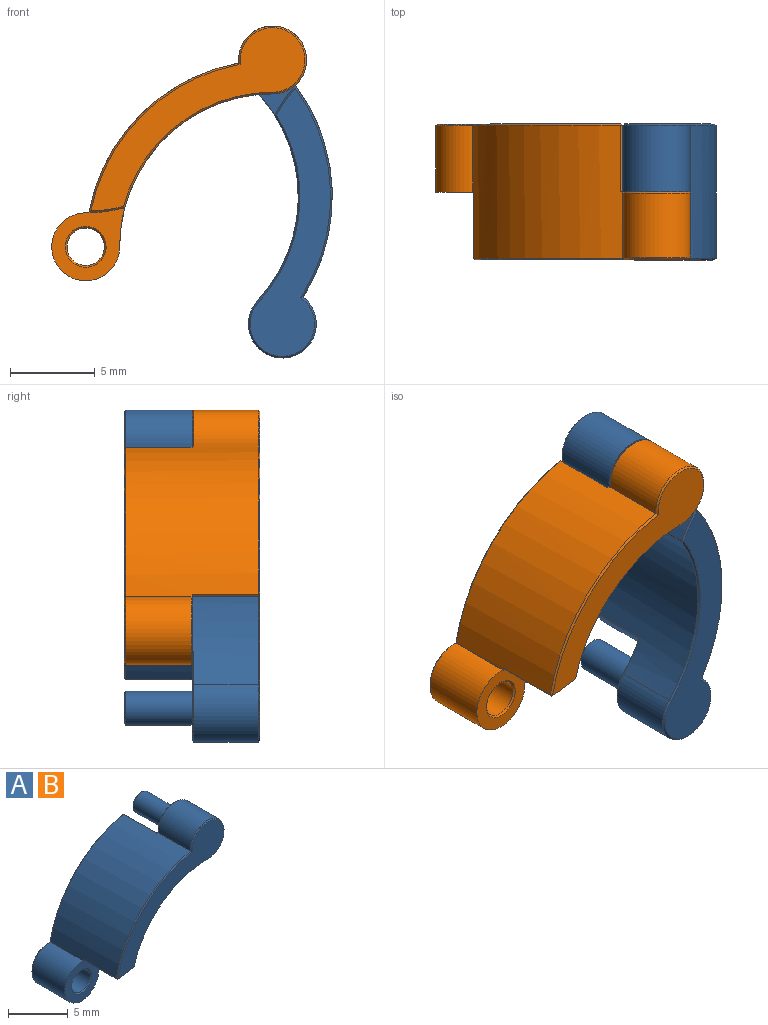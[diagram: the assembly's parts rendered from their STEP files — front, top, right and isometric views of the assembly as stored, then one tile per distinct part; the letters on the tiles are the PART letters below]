
ASSEMBLY  parts=2 mates=1
PART A: 38 faces, bbox 15x8x15 mm
  f0: cylinder r=2mm len=4mm, axis (0,1,0), area 36.5mm2, adj f1,f4,f23,f27
  f1: plane 3.9x0.11mm, normal (-0.18,0,0.98), area 0mm2, adj f0,f2,f6,f23,f28
  f2: cylinder r=11mm len=8.81mm, axis (0,1,0), area 102.4mm2, adj f1,f6,f7,f12,f15,f16,f31,f32
  f3: cylinder r=9mm len=3.9mm, axis (0,1,0), area 7.6mm2, adj f12,f30,f31,f35
  f4: cylinder r=9mm len=9mm, axis (0,1,0), area 91.5mm2, adj f0,f8,f12,f21,f24,f25,f29,f30
  f5: plane 12.59x10.79mm, normal (0,-1,0), area 33.1mm2, adj f27,f28,f29,f32,f35
  f6: plane 4.17x4.09mm, normal (0,1,0), area 9.5mm2, adj f1,f2,f9,f13,f15,f23,f25
  f7: plane 3.9x0.01mm, normal (-0.98,0,0.18), area 0mm2, adj f2,f8,f12,f17
  f8: cylinder r=2mm len=4mm, axis (0,-1,0), area 37.5mm2, adj f4,f7,f12,f19
  f9: cylinder r=9mm len=3.95mm, axis (0,-1,0), area 7.6mm2, adj f6,f15,f20,f24,f25
  f10: cylinder r=1.1mm len=3.8mm, axis (0,-1,0), area 26.3mm2, adj f26,f36
  f11: plane 12.59x10.79mm, normal (0,1,0), area 28.5mm2, adj f16,f17,f19,f20,f21,f26
  f12: plane 4.35x4.31mm, normal (0,-1,0), area 9.3mm2, adj f2,f3,f4,f7,f8,f30,f31,f36
  f13: cylinder r=1mm len=3.9mm, axis (0,-1,0), area 24.5mm2, adj f6,f37
  f14: plane 1.8x1.8mm, normal (0,1,0), area 2.5mm2, adj f37
  f15: plane 3.9x0.12mm, normal (0.65,0,0.76), area 0.6mm2, adj f2,f6,f9,f18
  f16: cone r=11mm half-angle=45deg, axis (0,-1,0), area 1.8mm2, adj f2,f11,f17,f18
  f17: plane 0.12x0.1mm, normal (-0.7,0.71,0.13), area 0mm2, adj f7,f11,f16,f19
  f18: plane 0.12x0.1mm, normal (0.55,0.53,0.65), area 0mm2, adj f15,f16,f20
  f19: cone r=2mm half-angle=45deg, axis (0,-1,0), area 1.3mm2, adj f8,f11,f17,f21
  f20: cone r=8.9mm half-angle=45deg, axis (0,-1,0), area 0.3mm2, adj f9,f11,f18,f22
  f21: cone r=9.1mm half-angle=45deg, axis (0,1,0), area 1.7mm2, adj f4,f11,f19,f22
  f22: plane 0.1x0.1mm, normal (0.54,0.65,-0.53), area 0mm2, adj f20,f21,f24
  f23: cone r=2mm half-angle=45deg, axis (0,-1,0), area 1.3mm2, adj f0,f1,f6,f25
  f24: plane 4x0.07mm, normal (0.71,0,-0.7), area 0.4mm2, adj f4,f9,f22,f25
  f25: cone r=9.1mm half-angle=45deg, axis (0,1,0), area 0.3mm2, adj f4,f6,f9,f23,f24
  f26: cone r=1.2mm half-angle=45deg, axis (0,1,0), area 1mm2, adj f10,f11
  f27: cone r=1.9mm half-angle=45deg, axis (0,1,0), area 1.3mm2, adj f0,f5,f28,f29
  f28: plane 0.12x0.1mm, normal (-0.13,-0.71,0.7), area 0mm2, adj f1,f5,f27,f32
  f29: cone r=9mm half-angle=45deg, axis (0,-1,0), area 1.7mm2, adj f4,f5,f27,f33
  f30: plane 3.9x0.07mm, normal (0.7,0,-0.71), area 0.4mm2, adj f3,f4,f12,f33
  f31: plane 3.9x0.12mm, normal (-0.76,0,-0.65), area 0.6mm2, adj f2,f3,f12,f34
  f32: cone r=10.9mm half-angle=45deg, axis (0,1,0), area 1.8mm2, adj f2,f5,f28,f34
  f33: plane 0.1x0.1mm, normal (0.53,-0.65,-0.54), area 0mm2, adj f29,f30,f35
  f34: plane 0.12x0.1mm, normal (-0.65,-0.53,-0.55), area 0mm2, adj f31,f32,f35
  f35: cone r=9mm half-angle=45deg, axis (0,1,0), area 0.3mm2, adj f3,f5,f33,f34
  f36: cone r=1.1mm half-angle=45deg, axis (0,-1,0), area 1mm2, adj f10,f12
  f37: cone r=1mm half-angle=45deg, axis (0,-1,0), area 0.8mm2, adj f13,f14
PART B: same geometry as A
PLACE A rot(axis=(0,1,0),132.9deg) t=(-13.2,-2.22,3.82)mm
PLACE B t=(-5.71,-2.22,0.88)mm fixed
MATE revolute B.f13 <-> A.f10  axis (0,1,0) through (-5.71,1.78,11.88)mm
